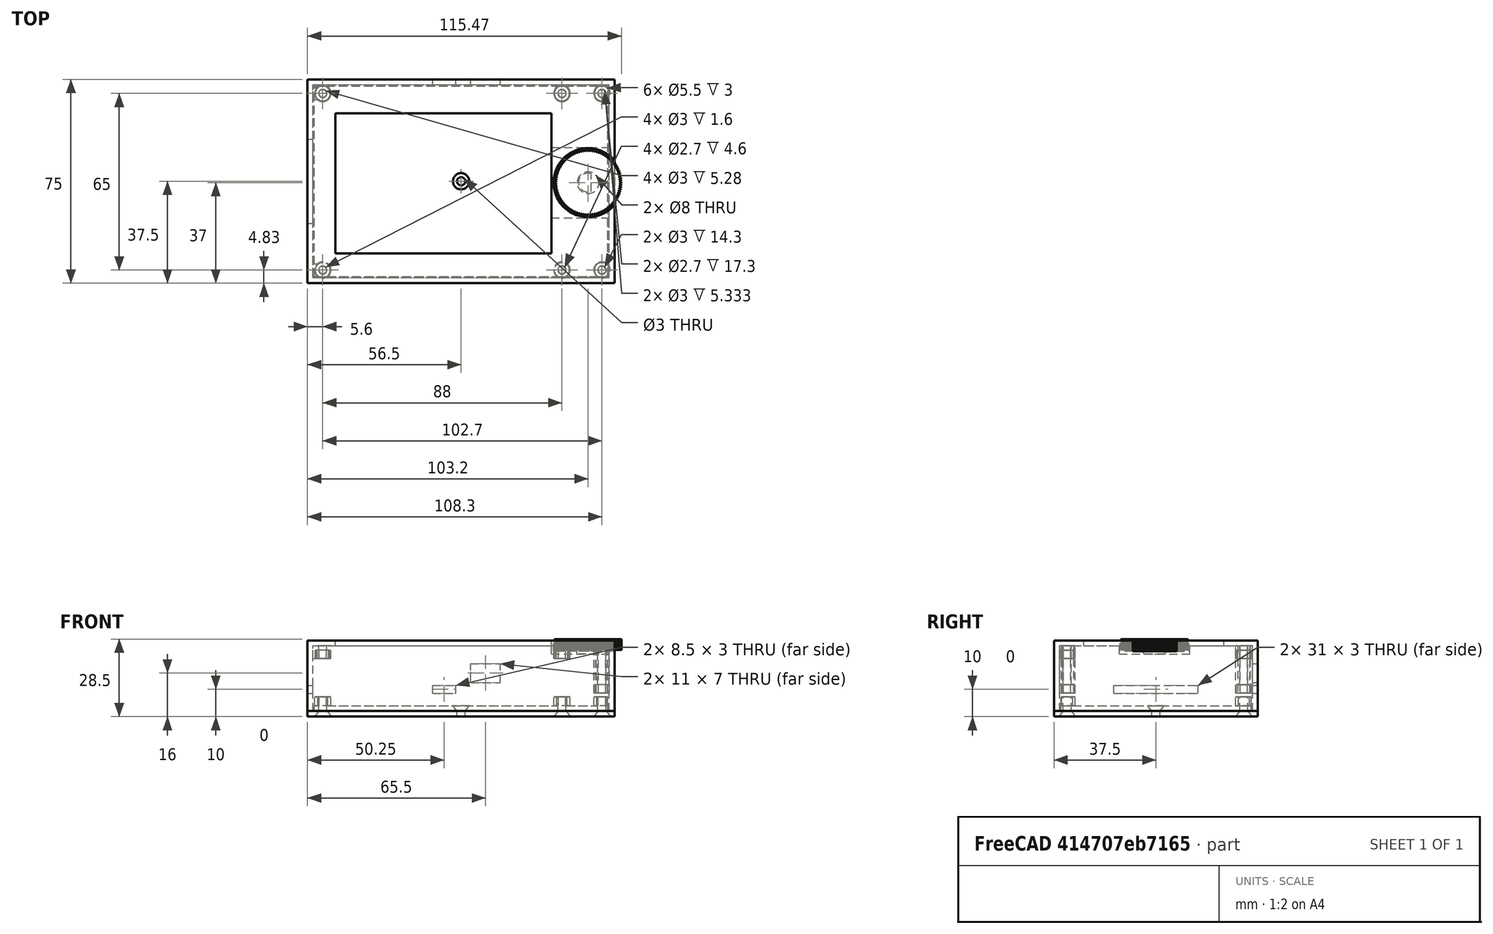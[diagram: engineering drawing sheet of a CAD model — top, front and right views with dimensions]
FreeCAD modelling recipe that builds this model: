
FCSTD DOCUMENT  (FreeCAD 0.18R16146 (Git))
Label: control_panel
License: All rights reserved
LicenseURL: http://en.wikipedia.org/wiki/All_rights_reserved
objects: Part::Cylinder×50, Part::Box×47, Part::Cut×38, Part::MultiFuse×15, Part::Cone×7, App::VRMLObject×1, Part::Part2DObjectPython×1, Part::Extrusion×1
note: 159 computed .brp shape members not serialized (recipe doc carries the construction recipe); baked Part::Feature solids carry a one-line shape summary decoded from their .brp

FEATURE [App::VRMLObject] mainboard
  Placement = pos=(-55,125,0) rot=(0,0,1;0rad)
FEATURE [Part::Box] Box  label="Würfel"
  AttacherType = Attacher::AttachEngine3D
  Height = 2
  Length = 109
  Placement = pos=(0,0,18) rot=(0,0,1;0rad)
  Width = 71
FEATURE [Part::Box] Box001  label="Würfel001"
  AttacherType = Attacher::AttachEngine3D
  Height = 2
  Length = 79.5
  Placement = pos=(8.2,9,18) rot=(0,0,1;0rad)
  Width = 51.5
FEATURE [Part::Cut] Cut
  Base = -> Box
  Tool = -> Box001
FEATURE [Part::Cylinder] Cylinder  label="Zylinder"
  Angle = 360
  AttacherType = Attacher::AttachEngine3D
  Height = 2
  Placement = pos=(101.2,35,18) rot=(0,0,1;0rad)
  Radius = 4
FEATURE [Part::Cut] Cut001
  Base = -> Cut
  Tool = -> Cylinder
FEATURE [Part::Cylinder] Cylinder001  label="Zylinder001"
  Angle = 360
  AttacherType = Attacher::AttachEngine3D
  Height = 4.7
  Placement = pos=(3.6,2.83,13.4) rot=(0,0,1;0rad)
  Radius = 3
FEATURE [Part::Cylinder] Cylinder002  label="Zylinder002"
  Angle = 360
  AttacherType = Attacher::AttachEngine3D
  Height = 4.7
  Placement = pos=(91.6,2.83,13.4) rot=(0,0,1;0rad)
  Radius = 3
FEATURE [Part::Cylinder] Cylinder003  label="Zylinder003"
  Angle = 360
  AttacherType = Attacher::AttachEngine3D
  Height = 4.7
  Placement = pos=(91.6,67.83,13.4) rot=(0,0,1;0rad)
  Radius = 3
FEATURE [Part::Cylinder] Cylinder004  label="Zylinder004"
  Angle = 360
  AttacherType = Attacher::AttachEngine3D
  Height = 4.7
  Placement = pos=(3.6,67.83,13.4) rot=(0,0,1;0rad)
  Radius = 3
FEATURE [Part::Cylinder] Cylinder005  label="Zylinder005"
  Angle = 360
  AttacherType = Attacher::AttachEngine3D
  Height = 18.8
  Placement = pos=(106.3,67.83,0.7) rot=(0,0,1;0rad)
  Radius = 3
FEATURE [Part::Cylinder] Cylinder006  label="Zylinder006"
  Angle = 360
  AttacherType = Attacher::AttachEngine3D
  Height = 18.8
  Placement = pos=(106.3,2.83,0.7) rot=(0,0,1;0rad)
  Radius = 3
FEATURE [Part::Cylinder] Cylinder007  label="Zylinder007"
  Angle = 360
  AttacherType = Attacher::AttachEngine3D
  Height = 4.7
  Placement = pos=(3.6,2.83,13.4) rot=(0,0,1;0rad)
  Radius = 1.5
FEATURE [Part::Cut] Cut002
  Base = -> Cylinder001
  Tool = -> Cylinder007
FEATURE [Part::Cylinder] Cylinder008  label="Zylinder008"
  Angle = 360
  AttacherType = Attacher::AttachEngine3D
  Height = 4.7
  Placement = pos=(91.6,2.83,13.4) rot=(0,0,1;0rad)
  Radius = 1.5
FEATURE [Part::Cut] Cut003
  Base = -> Cylinder002
  Tool = -> Cylinder008
FEATURE [Part::Cylinder] Cylinder009  label="Zylinder009"
  Angle = 360
  AttacherType = Attacher::AttachEngine3D
  Height = 4.7
  Placement = pos=(91.6,67.83,13.4) rot=(0,0,1;0rad)
  Radius = 1.5
FEATURE [Part::Cut] Cut004
  Base = -> Cylinder003
  Tool = -> Cylinder009
FEATURE [Part::Cylinder] Cylinder010  label="Zylinder010"
  Angle = 360
  AttacherType = Attacher::AttachEngine3D
  Height = 4.7
  Placement = pos=(3.6,67.83,13.4) rot=(0,0,1;0rad)
  Radius = 1.5
FEATURE [Part::Cut] Cut005
  Base = -> Cylinder004
  Tool = -> Cylinder010
FEATURE [Part::Cylinder] Cylinder011  label="Zylinder011"
  Angle = 360
  AttacherType = Attacher::AttachEngine3D
  Height = 18.8
  Placement = pos=(106.3,67.83,0.7) rot=(0,0,1;0rad)
  Radius = 1.5
FEATURE [Part::Cut] Cut006
  Base = -> Cylinder005
  Tool = -> Cylinder011
FEATURE [Part::Cylinder] Cylinder012  label="Zylinder012"
  Angle = 360
  AttacherType = Attacher::AttachEngine3D
  Height = 18.8
  Placement = pos=(106.3,2.83,0.7) rot=(0,0,1;0rad)
  Radius = 1.5
FEATURE [Part::Cut] Cut007
  Base = -> Cylinder006
  Tool = -> Cylinder012
FEATURE [Part::Box] Box002  label="Würfel002"
  AttacherType = Attacher::AttachEngine3D
  Height = 26
  Length = 2
  Placement = pos=(-2,0,-6) rot=(0,0,1;0rad)
  Width = 71
FEATURE [Part::Box] Box003  label="Würfel003"
  AttacherType = Attacher::AttachEngine3D
  Height = 26
  Length = 2
  Placement = pos=(109,0,-6) rot=(0,0,1;0rad)
  Width = 71
FEATURE [Part::Box] Box004  label="Würfel004"
  AttacherType = Attacher::AttachEngine3D
  Height = 26
  Length = 113
  Placement = pos=(-2,-2,-6) rot=(0,0,1;0rad)
  Width = 2
FEATURE [Part::Box] Box006  label="Würfel006"
  AttacherType = Attacher::AttachEngine3D
  Height = 3
  Length = 2
  Placement = pos=(-2,20,0.5) rot=(0,0,1;0rad)
  Width = 31
FEATURE [Part::Cut] Cut008
  Base = -> Box002
  Tool = -> Box006
FEATURE [Part::Box] Box007  label="Würfel007"
  AttacherType = Attacher::AttachEngine3D
  Height = 3
  Length = 8.5
  Placement = pos=(44,71,0.5) rot=(0,0,1;0rad)
  Width = 2
FEATURE [Part::Box] Box005  label="Würfel005"
  AttacherType = Attacher::AttachEngine3D
  Height = 26
  Length = 113
  Placement = pos=(-2,71,-6) rot=(0,0,1;0rad)
  Width = 2
FEATURE [Part::Cut] Cut009
  Base = -> Box005
  Tool = -> Box007
FEATURE [Part::Box] Box008  label="Würfel008"
  AttacherType = Attacher::AttachEngine3D
  Height = 7
  Length = 11
  Placement = pos=(58,71,4.5) rot=(0,0,1;0rad)
  Width = 2
FEATURE [Part::Cut] Cut010
  Base = -> Cut009
  Tool = -> Box008
FEATURE [Part::Box] Box009  label="Würfel009"
  AttacherType = Attacher::AttachEngine3D
  Height = 4.7
  Length = 4.5
  Placement = pos=(1.3,0,13.4) rot=(0,0,1;0rad)
  Width = 1
FEATURE [Part::Box] Box010  label="Würfel010"
  AttacherType = Attacher::AttachEngine3D
  Height = 18.8
  Length = 4.5
  Placement = pos=(104,70,0.7) rot=(0,0,1;0rad)
  Width = 1
FEATURE [Part::Box] Box011  label="Würfel011"
  AttacherType = Attacher::AttachEngine3D
  Height = 4.7
  Length = 4.5
  Placement = pos=(89.3,0,13.4) rot=(0,0,1;0rad)
  Width = 1
FEATURE [Part::Box] Box012  label="Würfel012"
  AttacherType = Attacher::AttachEngine3D
  Height = 4.7
  Length = 4.5
  Placement = pos=(1.3,70,13.4) rot=(0,0,1;0rad)
  Width = 1
FEATURE [Part::Box] Box013  label="Würfel013"
  AttacherType = Attacher::AttachEngine3D
  Height = 4.7
  Length = 4.5
  Placement = pos=(89.3,70,13.4) rot=(0,0,1;0rad)
  Width = 1
FEATURE [Part::Box] Box014  label="Würfel014"
  AttacherType = Attacher::AttachEngine3D
  Height = 18.8
  Length = 4.5
  Placement = pos=(104,0,0.7) rot=(0,0,1;0rad)
  Width = 1
FEATURE [Part::Box] Box015  label="Würfel015"
  AttacherType = Attacher::AttachEngine3D
  Height = 4.7
  Length = 1.7
  Placement = pos=(0,65.6,13.4) rot=(0,0,1;0rad)
  Width = 4.5
FEATURE [Part::Box] Box016  label="Würfel016"
  AttacherType = Attacher::AttachEngine3D
  Height = 4.7
  Length = 1.7
  Placement = pos=(0,0.6,13.4) rot=(0,0,1;0rad)
  Width = 4.5
FEATURE [Part::Box] Box017  label="Würfel017"
  AttacherType = Attacher::AttachEngine3D
  Height = 19.3
  Length = 1.7
  Placement = pos=(108,65.6,0.7) rot=(0,0,1;0rad)
  Width = 4.5
FEATURE [Part::Box] Box018  label="Würfel018"
  AttacherType = Attacher::AttachEngine3D
  Height = 19.3
  Length = 1.7
  Placement = pos=(108,0.6,0.7) rot=(0,0,1;0rad)
  Width = 4.5
FEATURE [Part::Cylinder] Cylinder013  label="Zylinder013"
  Angle = 360
  AttacherType = Attacher::AttachEngine3D
  Height = 3
  Placement = pos=(3.6,2.83,13.4) rot=(0,0,1;0rad)
  Radius = 2.75
FEATURE [Part::Cylinder] Cylinder014  label="Zylinder014"
  Angle = 360
  AttacherType = Attacher::AttachEngine3D
  Height = 3
  Placement = pos=(3.6,67.83,13.4) rot=(0,0,1;0rad)
  Radius = 2.75
FEATURE [Part::Cylinder] Cylinder015  label="Zylinder015"
  Angle = 360
  AttacherType = Attacher::AttachEngine3D
  Height = 3
  Placement = pos=(91.6,67.83,13.4) rot=(0,0,1;0rad)
  Radius = 2.75
FEATURE [Part::Cylinder] Cylinder016  label="Zylinder016"
  Angle = 360
  AttacherType = Attacher::AttachEngine3D
  Height = 3
  Placement = pos=(91.6,2.83,13.4) rot=(0,0,1;0rad)
  Radius = 2.75
FEATURE [Part::Cylinder] Cylinder017  label="Zylinder017"
  Angle = 360
  AttacherType = Attacher::AttachEngine3D
  Height = 3
  Placement = pos=(106.3,2.83,0.7) rot=(0,0,1;0rad)
  Radius = 2.75
FEATURE [Part::Cylinder] Cylinder018  label="Zylinder018"
  Angle = 360
  AttacherType = Attacher::AttachEngine3D
  Height = 3
  Placement = pos=(106.3,67.83,0.7) rot=(0,0,1;0rad)
  Radius = 2.75
FEATURE [Part::MultiFuse] Fusion
  Shapes = -> [Box004,Box003,Cut001,Cut008,Cut010]
FEATURE [Part::MultiFuse] Fusion001
  Shapes = -> [Box011,Box010,Box018,Box009,Box013,Box017,Box014,Box012,Box016,Box015,Fusion]
FEATURE [Part::MultiFuse] Fusion002
  Shapes = -> [Cut004,Cut007,Fusion001,Cut005,Cut006,Cut003,Cut002]
FEATURE [Part::Cut] Cut011
  Base = -> Fusion002
  Tool = -> Cylinder014
FEATURE [Part::Cut] Cut012
  Base = -> Cut011
  Tool = -> Cylinder015
FEATURE [Part::Cut] Cut013
  Base = -> Cut012
  Tool = -> Cylinder016
FEATURE [Part::Cut] Cut014
  Base = -> Cut013
  Tool = -> Cylinder013
FEATURE [Part::Cut] Cut015
  Base = -> Cut014
  Tool = -> Cylinder017
FEATURE [Part::Cut] Cut016  label="fusion8"
  Base = -> Cut015
  Tool = -> Cylinder018
FEATURE [Part::Box] Box019  label="Würfel019"
  AttacherType = Attacher::AttachEngine3D
  Height = 2
  Length = 108
  Placement = pos=(0.5,0.5,-6) rot=(0,0,1;0rad)
  Width = 70
FEATURE [Part::Box] Box020  label="Würfel020"
  AttacherType = Attacher::AttachEngine3D
  Height = 2
  Length = 113
  Placement = pos=(-2,-2,-8) rot=(0,0,1;0rad)
  Width = 75
FEATURE [Part::MultiFuse] Fusion003
  Shapes = -> [Box019,Box020]
FEATURE [Part::Cylinder] Cylinder019  label="Zylinder019"
  Angle = 360
  AttacherType = Attacher::AttachEngine3D
  Height = 3.2
  Placement = pos=(3.6,2.83,-4) rot=(0,0,1;0rad)
  Radius = 3
FEATURE [Part::Cylinder] Cylinder020  label="Zylinder020"
  Angle = 360
  AttacherType = Attacher::AttachEngine3D
  Height = 3.2
  Placement = pos=(91.6,2.83,-4) rot=(0,0,1;0rad)
  Radius = 3
FEATURE [Part::Cylinder] Cylinder021  label="Zylinder021"
  Angle = 360
  AttacherType = Attacher::AttachEngine3D
  Height = 3.2
  Placement = pos=(91.6,67.83,-4) rot=(0,0,1;0rad)
  Radius = 3
FEATURE [Part::Cylinder] Cylinder022  label="Zylinder022"
  Angle = 360
  AttacherType = Attacher::AttachEngine3D
  Height = 3.2
  Placement = pos=(3.6,67.83,-4) rot=(0,0,1;0rad)
  Radius = 3
FEATURE [Part::Cylinder] Cylinder023  label="Zylinder023"
  Angle = 360
  AttacherType = Attacher::AttachEngine3D
  Height = 3.2
  Placement = pos=(106.3,67.83,-4) rot=(0,0,1;0rad)
  Radius = 3
FEATURE [Part::Cylinder] Cylinder024  label="Zylinder024"
  Angle = 360
  AttacherType = Attacher::AttachEngine3D
  Height = 3.2
  Placement = pos=(106.3,2.83,-4) rot=(0,0,1;0rad)
  Radius = 3
FEATURE [Part::Cylinder] Cylinder025  label="Zylinder025"
  Angle = 360
  AttacherType = Attacher::AttachEngine3D
  Height = 7.2
  Placement = pos=(3.6,2.83,-8) rot=(0,0,1;0rad)
  Radius = 1.5
FEATURE [Part::Cylinder] Cylinder026  label="Zylinder026"
  Angle = 360
  AttacherType = Attacher::AttachEngine3D
  Height = 7.2
  Placement = pos=(91.6,2.83,-8) rot=(0,0,1;0rad)
  Radius = 1.5
FEATURE [Part::Cylinder] Cylinder027  label="Zylinder027"
  Angle = 360
  AttacherType = Attacher::AttachEngine3D
  Height = 7.2
  Placement = pos=(91.6,67.83,-8) rot=(0,0,1;0rad)
  Radius = 1.5
FEATURE [Part::Cylinder] Cylinder028  label="Zylinder028"
  Angle = 360
  AttacherType = Attacher::AttachEngine3D
  Height = 7.2
  Placement = pos=(3.6,67.83,-8) rot=(0,0,1;0rad)
  Radius = 1.5
FEATURE [Part::Cylinder] Cylinder029  label="Zylinder029"
  Angle = 360
  AttacherType = Attacher::AttachEngine3D
  Height = 7.2
  Placement = pos=(106.3,67.83,-8) rot=(0,0,1;0rad)
  Radius = 1.5
FEATURE [Part::Cylinder] Cylinder030  label="Zylinder030"
  Angle = 360
  AttacherType = Attacher::AttachEngine3D
  Height = 7.2
  Placement = pos=(106.3,2.83,-8) rot=(0,0,1;0rad)
  Radius = 1.5
FEATURE [Part::MultiFuse] Fusion004
  Shapes = -> [Cylinder019,Cylinder021,Cylinder022,Cylinder024,Cylinder023,Cylinder020]
FEATURE [Part::MultiFuse] Fusion005
  Shapes = -> [Cylinder027,Cylinder028,Cylinder029,Cylinder025,Cylinder030,Cylinder026]
FEATURE [Part::MultiFuse] Fusion006
  Shapes = -> [Fusion004,Fusion003]
FEATURE [Part::Cut] Cut017
  Base = -> Fusion006
  Tool = -> Fusion005
FEATURE [Part::Cone] Cone  label="Kegel"
  Angle = 360
  AttacherType = Attacher::AttachEngine3D
  Height = 2
  Placement = pos=(91.66,2.83,-6) rot=(0,1,0;3.14159rad)
  Radius1 = 1.5
  Radius2 = 3
FEATURE [Part::Cone] Cone001  label="Kegel001"
  Angle = 360
  AttacherType = Attacher::AttachEngine3D
  Height = 2
  Placement = pos=(3.66,2.83,-6) rot=(0,1,0;3.14159rad)
  Radius1 = 1.5
  Radius2 = 3
FEATURE [Part::Cone] Cone002  label="Kegel002"
  Angle = 360
  AttacherType = Attacher::AttachEngine3D
  Height = 2
  Placement = pos=(106.4,2.83,-6) rot=(0,1,0;3.14159rad)
  Radius1 = 1.5
  Radius2 = 3
FEATURE [Part::Cone] Cone003  label="Kegel003"
  Angle = 360
  AttacherType = Attacher::AttachEngine3D
  Height = 2
  Placement = pos=(91.66,67.83,-6) rot=(0,1,0;3.14159rad)
  Radius1 = 1.5
  Radius2 = 3
FEATURE [Part::Cone] Cone004  label="Kegel004"
  Angle = 360
  AttacherType = Attacher::AttachEngine3D
  Height = 2
  Placement = pos=(106.4,67.83,-6) rot=(0,1,0;3.14159rad)
  Radius1 = 1.5
  Radius2 = 3
FEATURE [Part::Cone] Cone005  label="Kegel005"
  Angle = 360
  AttacherType = Attacher::AttachEngine3D
  Height = 2
  Placement = pos=(3.66,67.83,-6) rot=(0,1,0;3.14159rad)
  Radius1 = 1.5
  Radius2 = 3
FEATURE [Part::MultiFuse] Fusion007
  Shapes = -> [Cone,Cone004,Cone003,Cone002,Cone005,Cone001]
FEATURE [Part::Cut] Cut018
  Base = -> Cut017
  Tool = -> Fusion007
FEATURE [Part::Cone] Cone006  label="Kegel006"
  Angle = 360
  AttacherType = Attacher::AttachEngine3D
  Height = 2
  Placement = pos=(0,0,2) rot=(0,1,0;0rad)
  Radius1 = 1.5
  Radius2 = 3
FEATURE [Part::Cylinder] Cylinder031  label="Zylinder031"
  Angle = 360
  AttacherType = Attacher::AttachEngine3D
  Height = 2
  Radius = 1.5
FEATURE [Part::MultiFuse] Fusion008
  Placement = pos=(54.5,35.5,-8) rot=(0,0,1;0rad)
  Shapes = -> [Cone006,Cylinder031]
FEATURE [Part::Cut] Cut019
  Base = -> Cut018
  Tool = -> Fusion008
FEATURE [Part::Box] Box021  label="Würfel021"
  AttacherType = Attacher::AttachEngine3D
  Height = 5.2
  Length = 2.5
  Placement = pos=(-2,0.5,-6) rot=(0,0,1;0rad)
  Width = 70
FEATURE [Part::Box] Box022  label="Würfel022"
  AttacherType = Attacher::AttachEngine3D
  Height = 5.2
  Length = 113
  Placement = pos=(-2,70.5,-6) rot=(0,0,1;0rad)
  Width = 2.5
FEATURE [Part::Box] Box023  label="Würfel023"
  AttacherType = Attacher::AttachEngine3D
  Height = 5.2
  Length = 2.5
  Placement = pos=(108.5,0.5,-6) rot=(0,0,1;0rad)
  Width = 70
FEATURE [Part::Box] Box024  label="Würfel024"
  AttacherType = Attacher::AttachEngine3D
  Height = 5.2
  Length = 113
  Placement = pos=(-2,-2,-6) rot=(0,0,1;0rad)
  Width = 2.5
FEATURE [Part::MultiFuse] Fusion009
  Shapes = -> [Box021,Box024,Box022,Box023]
FEATURE [Part::Cut] Cut020  label="bottom"
  Base = -> Cut019
  Tool = -> Fusion009
FEATURE [Part::Cylinder] Cylinder033  label="Zylinder033"
  Angle = 360
  AttacherType = Attacher::AttachEngine3D
  Height = 3
  Placement = pos=(101.2,35,20) rot=(0,0,1;0rad)
  Radius = 3.5
FEATURE [Part::Box] Box025  label="Würfel025"
  AttacherType = Attacher::AttachEngine3D
  Height = 3
  Length = 10
  Placement = pos=(102.3,30,20) rot=(0,0,1;0rad)
  Width = 10
FEATURE [Part::Cut] Cut021
  Base = -> Cylinder033
  Tool = -> Box025
FEATURE [Part::Part2DObjectPython] InvoluteGear  # Draft 2D object (typed FeaturePython)
  ExternalGear = true
  HighPrecision = true
  Modules = 0.266667
  NumberOfTeeth = 90
  Placement = pos=(101.2,35,20) rot=(0,0,1;0rad)
  PressureAngle = 20
FEATURE [Part::Extrusion] Extrude
  Base = -> InvoluteGear
  Dir = (0,0,1)
  DirMode = 0
  FaceMakerClass = Part::FaceMakerBullseye
  LengthFwd = 4
  LengthRev = 0
  Solid = true
  Symmetric = false
FEATURE [Part::Cut] Cut022  label="knob"
  Base = -> Extrude
  Placement = pos=(0,0,-3.5) rot=(0,0,1;0rad)
  Tool = -> Cut021
FEATURE [Part::Cylinder] Cylinder034  label="Zylinder034"
  Angle = 360
  AttacherType = Attacher::AttachEngine3D
  Height = 5
  Placement = pos=(101.2,35,15) rot=(0,0,1;0rad)
  Radius = 4
FEATURE [Part::Box] Box026  label="Würfel026"
  AttacherType = Attacher::AttachEngine3D
  Height = 5
  Length = 21.3
  Placement = pos=(87.7,22,15) rot=(0,0,1;0rad)
  Width = 26
FEATURE [Part::Cylinder] Cylinder035  label="Zylinder035"
  Angle = 360
  AttacherType = Attacher::AttachEngine3D
  Height = 4
  Placement = pos=(101.2,35,16) rot=(0,0,1;0rad)
  Radius = 12.7
FEATURE [Part::MultiFuse] Fusion010
  Shapes = -> [Box026,Cut016]
FEATURE [Part::Cut] Cut023
  Base = -> Fusion010
  Tool = -> Cylinder035
FEATURE [Part::Cut] Cut024  label="top_threaded_insert"
  Base = -> Cut023
  Tool = -> Cylinder034
FEATURE [Part::Box] Box027  label="Würfel027"
  AttacherType = Attacher::AttachEngine3D
  Height = 4.7
  Length = 1.7
  Placement = pos=(0,0.6,13.4) rot=(0,0,1;0rad)
  Width = 4.5
FEATURE [Part::Box] Box028  label="Würfel028"
  AttacherType = Attacher::AttachEngine3D
  Height = 18.8
  Length = 4.5
  Placement = pos=(104,0,0.7) rot=(0,0,1;0rad)
  Width = 1
FEATURE [Part::Cylinder] Cylinder037  label="Zylinder037"
  Angle = 360
  AttacherType = Attacher::AttachEngine3D
  Height = 5
  Placement = pos=(101.2,35,15) rot=(0,0,1;0rad)
  Radius = 4
FEATURE [Part::Cylinder] Cylinder038  label="Zylinder038"
  Angle = 360
  AttacherType = Attacher::AttachEngine3D
  Height = 4.7
  Placement = pos=(3.6,2.83,13.4) rot=(0,0,1;0rad)
  Radius = 3
FEATURE [Part::Box] Box029  label="Würfel029"
  AttacherType = Attacher::AttachEngine3D
  Height = 5
  Length = 21.3
  Placement = pos=(87.7,22,15) rot=(0,0,1;0rad)
  Width = 26
FEATURE [Part::Box] Box030  label="Würfel030"
  AttacherType = Attacher::AttachEngine3D
  Height = 26
  Length = 113
  Placement = pos=(-2,71,-6) rot=(0,0,1;0rad)
  Width = 2
FEATURE [Part::Box] Box031  label="Würfel031"
  AttacherType = Attacher::AttachEngine3D
  Height = 4.7
  Length = 1.7
  Placement = pos=(0,65.6,13.4) rot=(0,0,1;0rad)
  Width = 4.5
FEATURE [Part::Box] Box032  label="Würfel032"
  AttacherType = Attacher::AttachEngine3D
  Height = 4.7
  Length = 4.5
  Placement = pos=(1.3,70,13.4) rot=(0,0,1;0rad)
  Width = 1
FEATURE [Part::Cylinder] Cylinder040  label="Zylinder040"
  Angle = 360
  AttacherType = Attacher::AttachEngine3D
  Height = 4.7
  Placement = pos=(91.6,2.83,13.4) rot=(0,0,1;0rad)
  Radius = 1.35
FEATURE [Part::Box] Box033  label="Würfel033"
  AttacherType = Attacher::AttachEngine3D
  Height = 19.3
  Length = 1.7
  Placement = pos=(108,0.6,0.7) rot=(0,0,1;0rad)
  Width = 4.5
FEATURE [Part::Cylinder] Cylinder041  label="Zylinder041"
  Angle = 360
  AttacherType = Attacher::AttachEngine3D
  Height = 4.7
  Placement = pos=(3.6,67.83,13.4) rot=(0,0,1;0rad)
  Radius = 3
FEATURE [Part::Box] Box034  label="Würfel034"
  AttacherType = Attacher::AttachEngine3D
  Height = 19.3
  Length = 1.7
  Placement = pos=(108,65.6,0.7) rot=(0,0,1;0rad)
  Width = 4.5
FEATURE [Part::Cylinder] Cylinder042  label="Zylinder042"
  Angle = 360
  AttacherType = Attacher::AttachEngine3D
  Height = 4.7
  Placement = pos=(91.6,67.83,13.4) rot=(0,0,1;0rad)
  Radius = 1.35
FEATURE [Part::Box] Box035  label="Würfel035"
  AttacherType = Attacher::AttachEngine3D
  Height = 3
  Length = 8.5
  Placement = pos=(44,71,0.5) rot=(0,0,1;0rad)
  Width = 2
FEATURE [Part::Cut] Cut025
  Base = -> Box030
  Tool = -> Box035
FEATURE [Part::Cylinder] Cylinder044  label="Zylinder044"
  Angle = 360
  AttacherType = Attacher::AttachEngine3D
  Height = 18.8
  Placement = pos=(106.3,2.83,0.7) rot=(0,0,1;0rad)
  Radius = 3
FEATURE [Part::Box] Box036  label="Würfel036"
  AttacherType = Attacher::AttachEngine3D
  Height = 26
  Length = 2
  Placement = pos=(109,0,-6) rot=(0,0,1;0rad)
  Width = 71
FEATURE [Part::Cylinder] Cylinder045  label="Zylinder045"
  Angle = 360
  AttacherType = Attacher::AttachEngine3D
  Height = 4
  Placement = pos=(101.2,35,16) rot=(0,0,1;0rad)
  Radius = 12.7
FEATURE [Part::Cylinder] Cylinder046  label="Zylinder046"
  Angle = 360
  AttacherType = Attacher::AttachEngine3D
  Height = 18.8
  Placement = pos=(106.3,67.83,0.7) rot=(0,0,1;0rad)
  Radius = 1.35
FEATURE [Part::Cylinder] Cylinder047  label="Zylinder047"
  Angle = 360
  AttacherType = Attacher::AttachEngine3D
  Height = 4.7
  Placement = pos=(91.6,2.83,13.4) rot=(0,0,1;0rad)
  Radius = 3
FEATURE [Part::Cut] Cut030
  Base = -> Cylinder047
  Tool = -> Cylinder040
FEATURE [Part::Box] Box037  label="Würfel037"
  AttacherType = Attacher::AttachEngine3D
  Height = 18.8
  Length = 4.5
  Placement = pos=(104,70,0.7) rot=(0,0,1;0rad)
  Width = 1
FEATURE [Part::Box] Box038  label="Würfel038"
  AttacherType = Attacher::AttachEngine3D
  Height = 4.7
  Length = 4.5
  Placement = pos=(89.3,70,13.4) rot=(0,0,1;0rad)
  Width = 1
FEATURE [Part::Box] Box039  label="Würfel039"
  AttacherType = Attacher::AttachEngine3D
  Height = 26
  Length = 2
  Placement = pos=(-2,0,-6) rot=(0,0,1;0rad)
  Width = 71
FEATURE [Part::Cylinder] Cylinder050  label="Zylinder050"
  Angle = 360
  AttacherType = Attacher::AttachEngine3D
  Height = 4.7
  Placement = pos=(3.6,2.83,13.4) rot=(0,0,1;0rad)
  Radius = 1.35
FEATURE [Part::Cut] Cut034
  Base = -> Cylinder038
  Tool = -> Cylinder050
FEATURE [Part::Box] Box040  label="Würfel040"
  AttacherType = Attacher::AttachEngine3D
  Height = 4.7
  Length = 4.5
  Placement = pos=(89.3,0,13.4) rot=(0,0,1;0rad)
  Width = 1
FEATURE [Part::Box] Box041  label="Würfel041"
  AttacherType = Attacher::AttachEngine3D
  Height = 7
  Length = 11
  Placement = pos=(58,71,4.5) rot=(0,0,1;0rad)
  Width = 2
FEATURE [Part::Cut] Cut029
  Base = -> Cut025
  Tool = -> Box041
FEATURE [Part::Box] Box042  label="Würfel042"
  AttacherType = Attacher::AttachEngine3D
  Height = 4.7
  Length = 4.5
  Placement = pos=(1.3,0,13.4) rot=(0,0,1;0rad)
  Width = 1
FEATURE [Part::Box] Box043  label="Würfel043"
  AttacherType = Attacher::AttachEngine3D
  Height = 2
  Length = 109
  Placement = pos=(0,0,18) rot=(0,0,1;0rad)
  Width = 71
FEATURE [Part::Box] Box044  label="Würfel044"
  AttacherType = Attacher::AttachEngine3D
  Height = 3
  Length = 2
  Placement = pos=(-2,20,0.5) rot=(0,0,1;0rad)
  Width = 31
FEATURE [Part::Cut] Cut039
  Base = -> Box039
  Tool = -> Box044
FEATURE [Part::Cylinder] Cylinder052  label="Zylinder052"
  Angle = 360
  AttacherType = Attacher::AttachEngine3D
  Height = 4.7
  Placement = pos=(91.6,67.83,13.4) rot=(0,0,1;0rad)
  Radius = 3
FEATURE [Part::Cut] Cut033
  Base = -> Cylinder052
  Tool = -> Cylinder042
FEATURE [Part::Cylinder] Cylinder053  label="Zylinder053"
  Angle = 360
  AttacherType = Attacher::AttachEngine3D
  Height = 18.8
  Placement = pos=(106.3,2.83,0.7) rot=(0,0,1;0rad)
  Radius = 1.35
FEATURE [Part::Cut] Cut037
  Base = -> Cylinder044
  Tool = -> Cylinder053
FEATURE [Part::Box] Box045  label="Würfel045"
  AttacherType = Attacher::AttachEngine3D
  Height = 26
  Length = 113
  Placement = pos=(-2,-2,-6) rot=(0,0,1;0rad)
  Width = 2
FEATURE [Part::Box] Box046  label="Würfel046"
  AttacherType = Attacher::AttachEngine3D
  Height = 2
  Length = 79.5
  Placement = pos=(8.2,9,18) rot=(0,0,1;0rad)
  Width = 51.5
FEATURE [Part::Cut] Cut036
  Base = -> Box043
  Tool = -> Box046
FEATURE [Part::Cylinder] Cylinder054  label="Zylinder054"
  Angle = 360
  AttacherType = Attacher::AttachEngine3D
  Height = 2
  Placement = pos=(101.2,35,18) rot=(0,0,1;0rad)
  Radius = 4
FEATURE [Part::Cylinder] Cylinder055  label="Zylinder055"
  Angle = 360
  AttacherType = Attacher::AttachEngine3D
  Height = 18.8
  Placement = pos=(106.3,67.83,0.7) rot=(0,0,1;0rad)
  Radius = 3
FEATURE [Part::Cut] Cut035
  Base = -> Cylinder055
  Tool = -> Cylinder046
FEATURE [Part::Cylinder] Cylinder056  label="Zylinder056"
  Angle = 360
  AttacherType = Attacher::AttachEngine3D
  Height = 4.7
  Placement = pos=(3.6,67.83,13.4) rot=(0,0,1;0rad)
  Radius = 1.35
FEATURE [Part::Cut] Cut032
  Base = -> Cylinder041
  Tool = -> Cylinder056
FEATURE [Part::Cut] Cut043
  Base = -> Cut036
  Tool = -> Cylinder054
FEATURE [Part::MultiFuse] Fusion014
  Shapes = -> [Box045,Box036,Cut043,Cut039,Cut029]
FEATURE [Part::MultiFuse] Fusion012
  Shapes = -> [Box040,Box037,Box033,Box042,Box038,Box034,Box028,Box032,Box027,Box031,Fusion014]
FEATURE [Part::MultiFuse] Fusion013
  Shapes = -> [Cut033,Cut037,Fusion012,Cut032,Cut035,Cut030,Cut034]
FEATURE [Part::MultiFuse] Fusion011
  Shapes = -> [Box029,Fusion013]
FEATURE [Part::Cut] Cut041
  Base = -> Fusion011
  Tool = -> Cylinder045
FEATURE [Part::Cut] Cut040  label="top_screw_in"
  Base = -> Cut041
  Tool = -> Cylinder037
